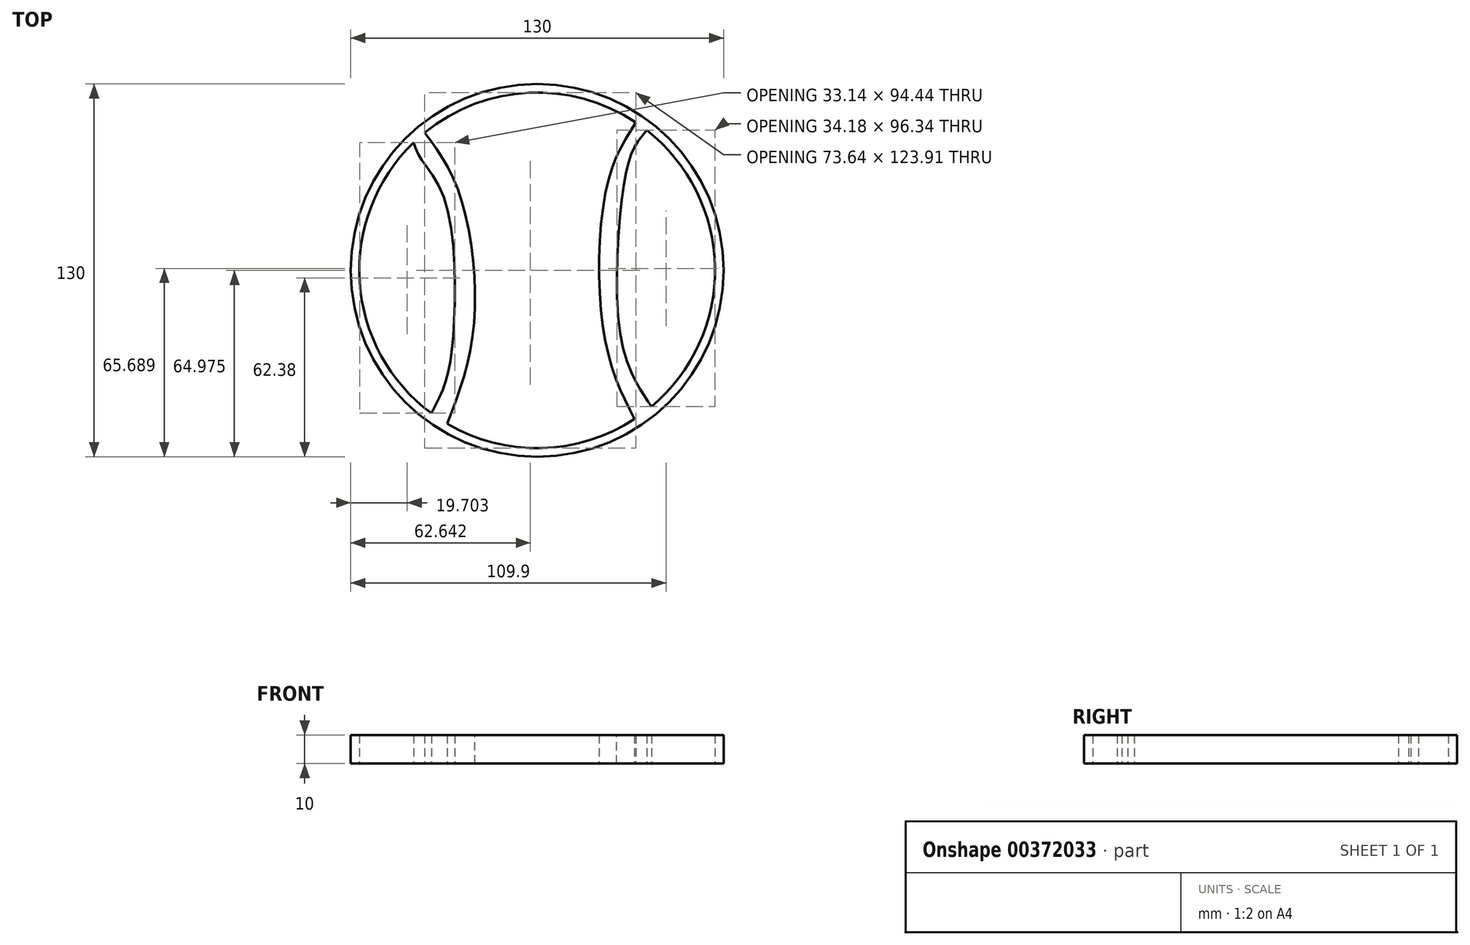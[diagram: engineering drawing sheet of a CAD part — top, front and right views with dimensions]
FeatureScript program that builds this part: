
annotation { "Feature Type Name" : "Feature", "Feature Type Description" : "" }
export const myFeature = defineFeature(function(context is Context, id is Id, definition is map)
    precondition{}
    {
        {
            var Q0;
            Q0=qCreatedBy(makeId("Top.planeOp"),FACE);
            var sketch = newSketch(context, id + "F0", { "sketchPlane" : qUnion([Q0])});
            skCircle(sketch, "E0", {"center": v(0, 0) * mm, "radius": 65 * mm});
            skArc(sketch, "E1", {"start": v(-43.07, 44.6) * mm, "mid": v(-61.87, -4.06) * mm, "end": v(-36.87, -49.84) * mm});
            skFitSpline(sketch, "E2", {"points": [v(-39.18, 48.05) * mm, v(-27, 26.4) * mm, v(-22.19, -20.18) * mm, v(-31.34, -53.5) * mm], "startDerivative": vector(47.76, -65.65) * mm, "endDerivative": vector(-35.34, -92.1) * mm});
            skFitSpline(sketch, "E3", {"points": [v(34.46, 51.54) * mm, v(24.5, 30.14) * mm, v(23.72, -24.4) * mm, v(33.97, -51.87) * mm], "startDerivative": vector(-41.34, -63.68) * mm, "endDerivative": vector(39.13, -76.3) * mm});
            skFitSpline(sketch, "E4", {"points": [v(38.17, 48.86) * mm, v(33.97, 42.98) * mm, v(30.04, 28.75) * mm, v(29.05, -23.02) * mm, v(36.17, -41.8) * mm, v(39.87, -47.48) * mm], "startDerivative": vector(-34.47, -42.2) * mm, "endDerivative": vector(27.55, -40.75) * mm});
            skFitSpline(sketch, "E5", {"points": [v(-43.07, 44.6) * mm, v(-40.7, 39.23) * mm, v(-32.4, 25.2) * mm, v(-29.05, -19.66) * mm, v(-32.2, -39.62) * mm, v(-36.87, -49.84) * mm], "startDerivative": vector(14.62, -44.53) * mm, "endDerivative": vector(-31.77, -60.63) * mm});
            skArc(sketch, "E6.trimOffspring", {"start": v(34.46, 51.54) * mm, "mid": v(-2.93, 61.93) * mm, "end": v(-39.18, 48.05) * mm});
            skArc(sketch, "E7.trimOffspring", {"start": v(39.87, -47.48) * mm, "mid": v(62, 1.1) * mm, "end": v(38.17, 48.86) * mm});
            skArc(sketch, "E8.trimOffspring", {"start": v(-31.34, -53.5) * mm, "mid": v(1.55, -61.98) * mm, "end": v(33.97, -51.87) * mm});
            skSolve(sketch);
        }
        {
            var Q0;
            Q0 = qSketchRegion(id + "F0", true);
            extrude(context, id + "F1", {"entities" : qUnion([Q0]), "depth" : 10 * mm});
        }
    });
